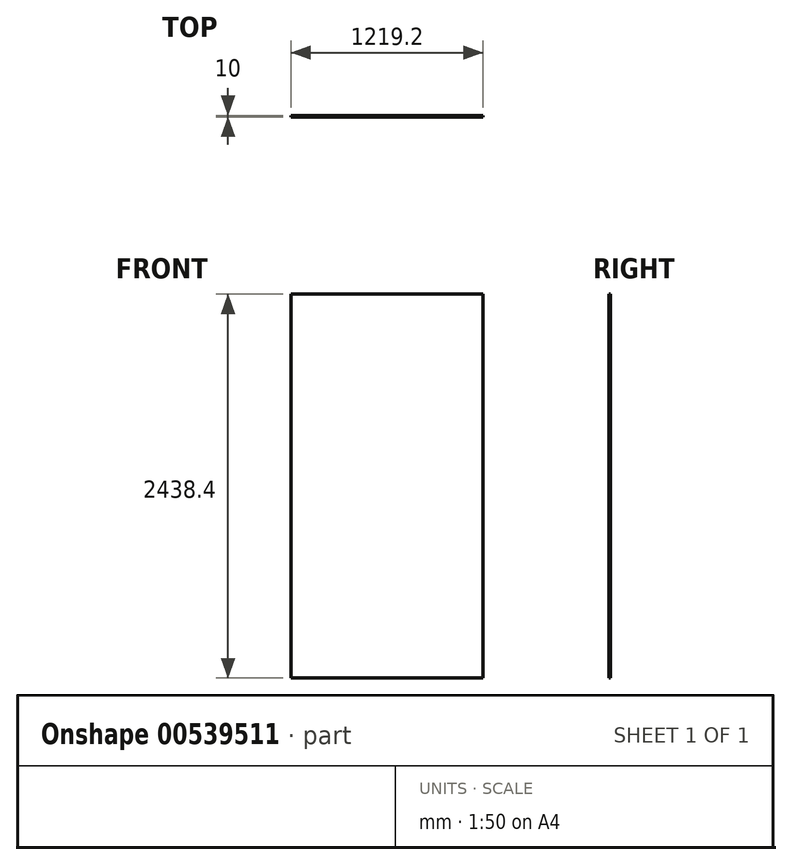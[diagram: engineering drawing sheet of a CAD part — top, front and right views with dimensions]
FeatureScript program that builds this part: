
annotation { "Feature Type Name" : "Feature", "Feature Type Description" : "" }
export const myFeature = defineFeature(function(context is Context, id is Id, definition is map)
    precondition{}
    {
        {
            var Q0;
            Q0=qCreatedBy(makeId("Front.planeOp"),FACE);
            var sketch = newSketch(context, id + "F0", { "sketchPlane" : qUnion([Q0])});
            skLineSegment(sketch, "E0.bottom", {"start": v(609.6, -1219.2) * mm, "end": v(-609.6, -1219.2) * mm});
            skLineSegment(sketch, "E0.top", {"start": v(609.6, 1219.2) * mm, "end": v(-609.6, 1219.2) * mm});
            skLineSegment(sketch, "E0.left", {"start": v(609.6, -1219.2) * mm, "end": v(609.6, 1219.2) * mm});
            skLineSegment(sketch, "E0.right", {"start": v(-609.6, -1219.2) * mm, "end": v(-609.6, 1219.2) * mm});
            skPoint(sketch, "E0.middle", {"position": v(0, 0) * mm});
            skSolve(sketch);
        }
        {
            var Q0;
            Q0=makeQuery(id+"F0.imprint","IMPRINT",FACE,{"disambiguationData":[TD([[makeQuery(id+"F0.imprint","IMPRINT",EDGE,{"derivedFrom":sQuery(id+"F0.wireOp",EDGE,"E0.bottom")}),-1.0]])]});
            extrude(context, id + "F1", {"entities" : qUnion([Q0]), "depth" : 10 * mm});
        }
    });
